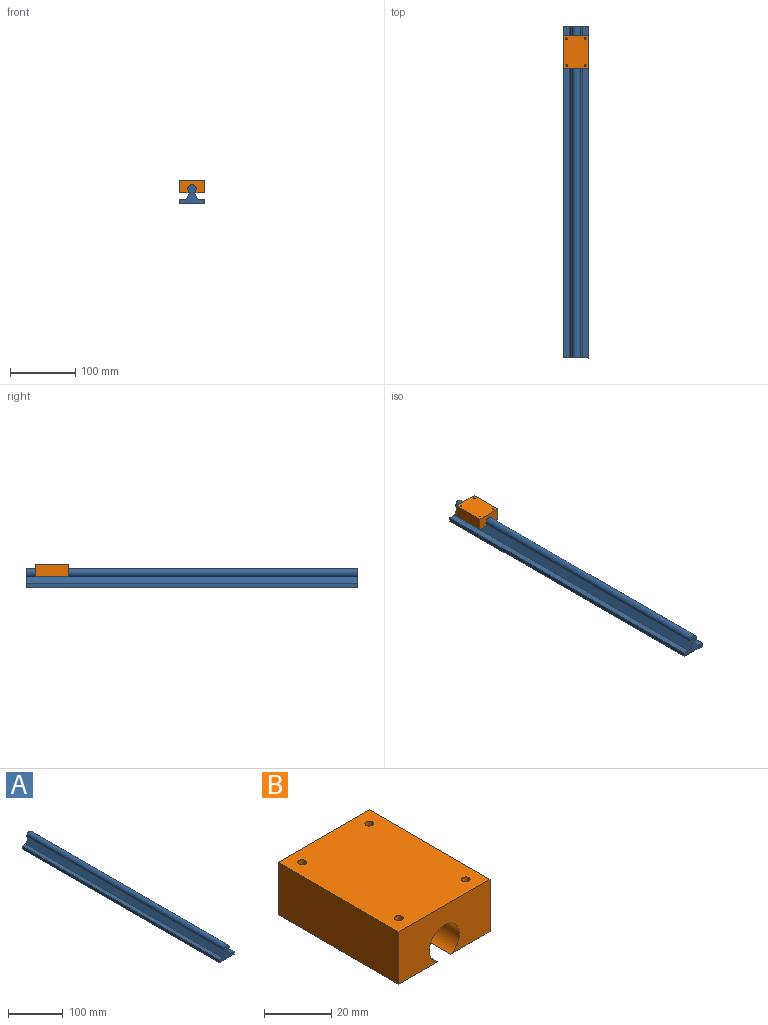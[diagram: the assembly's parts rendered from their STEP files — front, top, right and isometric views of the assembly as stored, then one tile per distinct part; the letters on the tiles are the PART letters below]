
ASSEMBLY  parts=2 mates=1
PART A: 10 faces, bbox 38.1x508x29.2 mm
  f0: cylinder r=6.35mm len=508mm, axis (0,1,0), area 17373.8mm2, adj f1,f7,f8,f9
  f1: plane 508x10.74mm, normal (-0.85,0,0.53), area 6451.6mm2, adj f0,f2,f8,f9
  f2: plane 508x9.53mm, normal (0,0,1), area 4838.7mm2, adj f1,f3,f8,f9
  f3: plane 508x6.35mm, normal (-1,0,0), area 3225.8mm2, adj f2,f4,f8,f9
  f4: plane 508x38.1mm, normal (0,0,-1), area 19354.8mm2, adj f3,f5,f8,f9
  f5: plane 508x6.35mm, normal (1,0,0), area 3225.8mm2, adj f4,f6,f8,f9
  f6: plane 508x9.53mm, normal (0,0,1), area 4838.7mm2, adj f5,f7,f8,f9
  f7: plane 508x10.74mm, normal (0.85,0,0.53), area 6451.6mm2, adj f0,f6,f8,f9
  f8: plane 38.1x29.17mm, normal (0,-1,0), area 498.2mm2, adj f0,f1,f2,f3,f4,f5,f6,f7
  f9: plane 38.1x29.17mm, normal (0,1,0), area 498.2mm2, adj f0,f1,f2,f3,f4,f5,f6,f7
PART B: 16 faces, bbox 38.4x50.8x19.1 mm
  f0: plane 50.8x16.43mm, normal (0,0,-1), area 834.5mm2, adj f1,f5,f6,f7
  f1: plane 50.8x19.05mm, normal (1,0,0), area 967.7mm2, adj f0,f2,f6,f7
  f2: plane 50.8x38.37mm, normal (0,0,1), area 1928.8mm2, adj f1,f3,f6,f7,f8,f10,f12,f14
  f3: plane 50.8x19.05mm, normal (-1,0,0), area 967.7mm2, adj f2,f4,f6,f7
  f4: plane 50.8x16.43mm, normal (0,0,-1), area 834.5mm2, adj f3,f5,f6,f7
  f5: cylinder r=6.35mm len=50.8mm, axis (0,1,0), area 1737.2mm2, adj f0,f4,f6,f7
  f6: plane 38.37x19.05mm, normal (0,-1,0), area 606.6mm2, adj f0,f1,f2,f3,f4,f5
  f7: plane 38.37x19.05mm, normal (0,1,0), area 606.6mm2, adj f0,f1,f2,f3,f4,f5
  f8: cylinder r=1.27mm len=12.7mm, axis (0,0,1), area 101.3mm2, adj f2,f9
  f9: plane 2.54x2.54mm, normal (0,0,1), area 5.1mm2, adj f8
  f10: cylinder r=1.27mm len=12.7mm, axis (0,0,1), area 101.3mm2, adj f2,f11
  f11: plane 2.54x2.54mm, normal (0,0,1), area 5.1mm2, adj f10
  f12: cylinder r=1.27mm len=12.7mm, axis (0,0,1), area 101.3mm2, adj f2,f13
  f13: plane 2.54x2.54mm, normal (0,0,1), area 5.1mm2, adj f12
  f14: cylinder r=1.27mm len=12.7mm, axis (0,0,1), area 101.3mm2, adj f2,f15
  f15: plane 2.54x2.54mm, normal (0,0,1), area 5.1mm2, adj f14
PLACE A t=(-175.22,-101.03,219.42)mm
PLACE B t=(-168.88,-115.52,213.59)mm
MATE slider B.f5 <-> A.f0  axis (0,-1,0) through (-199.5,-166.32,229.39)mm
